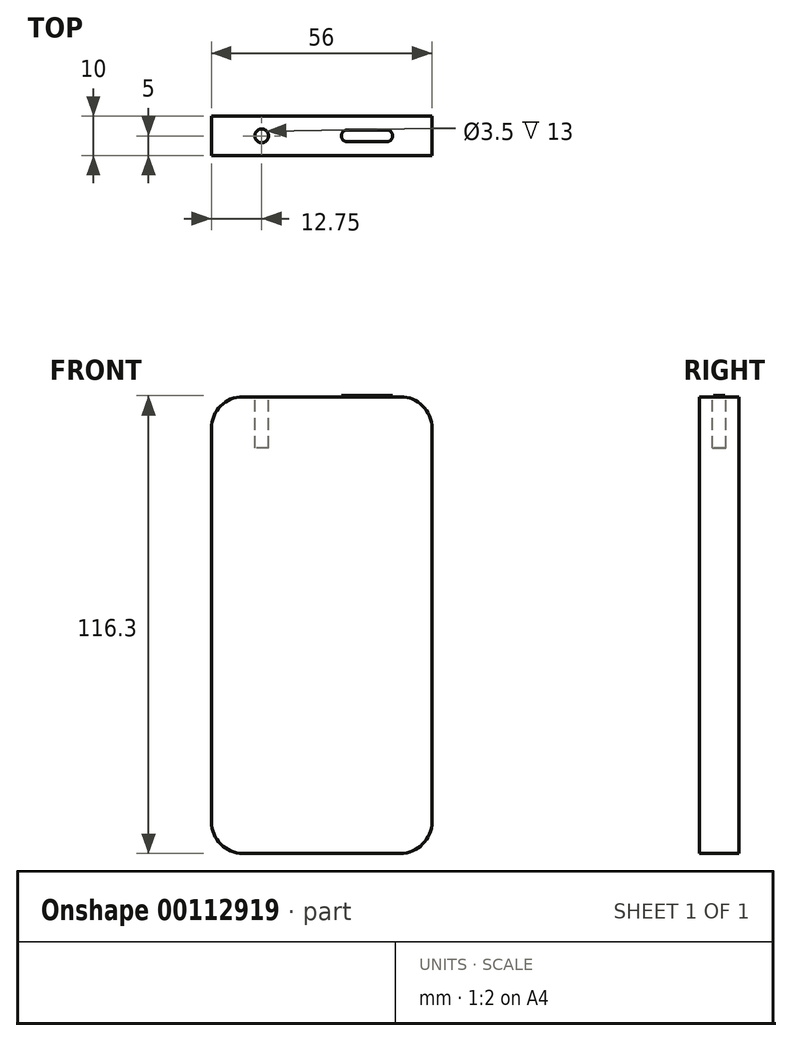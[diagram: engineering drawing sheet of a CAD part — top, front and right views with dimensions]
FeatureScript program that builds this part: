
annotation { "Feature Type Name" : "Feature", "Feature Type Description" : "" }
export const myFeature = defineFeature(function(context is Context, id is Id, definition is map)
    precondition{}
    {
        {
            var Q0;
            Q0=qCreatedBy(makeId("Front.planeOp"),FACE);
            var sketch = newSketch(context, id + "F0", { "sketchPlane" : qUnion([Q0])});
            skLineSegment(sketch, "E0.bottom", {"start": v(28, -58) * mm, "end": v(-28, -58) * mm});
            skLineSegment(sketch, "E0.top", {"start": v(28, 58) * mm, "end": v(-28, 58) * mm});
            skLineSegment(sketch, "E0.left", {"start": v(28, -58) * mm, "end": v(28, 58) * mm});
            skLineSegment(sketch, "E0.right", {"start": v(-28, -58) * mm, "end": v(-28, 58) * mm});
            skPoint(sketch, "E0.middle", {"position": v(0, 0) * mm});
            skSolve(sketch);
        }
        {
            var Q0;
            Q0 = qSketchRegion(id + "F0", true);
            extrude(context, id + "F1", {"entities" : qUnion([Q0]), "endBound" : BoundingType.SYMMETRIC, "depth" : 10 * mm});
        }
        {
            var Q0;
            Q0=makeQuery(id+"F1.opExtrude","SWEPT_EDGE",EDGE,{"disambiguationData":[OSD([sQuery(id+"F0.wireOp",EDGE,"E0.top"),sQuery(id+"F0.wireOp",EDGE,"E0.right")])]});
            var Q1;
            Q1=makeQuery(id+"F1.opExtrude","SWEPT_EDGE",EDGE,{"disambiguationData":[OSD([sQuery(id+"F0.wireOp",EDGE,"E0.top"),sQuery(id+"F0.wireOp",EDGE,"E0.left")])]});
            var Q2;
            Q2=makeQuery(id+"F1.opExtrude","SWEPT_EDGE",EDGE,{"disambiguationData":[OSD([sQuery(id+"F0.wireOp",EDGE,"E0.bottom"),sQuery(id+"F0.wireOp",EDGE,"E0.left")])]});
            var Q3;
            Q3=makeQuery(id+"F1.opExtrude","SWEPT_EDGE",EDGE,{"disambiguationData":[OSD([sQuery(id+"F0.wireOp",EDGE,"E0.bottom"),sQuery(id+"F0.wireOp",EDGE,"E0.right")])]});
            fillet(context, id + "F2", {"entities" : qUnion([Q0, Q1, Q2, Q3]), "radius" : 8 * mm, "tangentPropagation" : true, "allowEdgeOverflow" : false});
        }
        {
            var Q0;
            Q0=makeQuery(id+"F1.opExtrude","SWEPT_FACE",FACE,{"disambiguationData":[OSD([sQuery(id+"F0.wireOp",EDGE,"E0.top")])]});
            var sketch = newSketch(context, id + "F3", { "sketchPlane" : qUnion([Q0])});
            skCircle(sketch, "E1", {"center": v(-15.25, 0) * mm, "radius": 1.75 * mm});
            skSolve(sketch);
        }
        {
            var Q0;
            Q0 = qSketchRegion(id + "F3", true);
            extrude(context, id + "F4", {"entities" : qUnion([Q0]), "operationType" : NewBodyOperationType.REMOVE, "oppositeDirection" : true, "depth" : 13 * mm});
        }
        {
            var Q0;
            Q0=makeQuery(id+"F1.opExtrude","SWEPT_FACE",FACE,{"disambiguationData":[OSD([sQuery(id+"F0.wireOp",EDGE,"E0.top")])]});
            var sketch = newSketch(context, id + "F5", { "sketchPlane" : qUnion([Q0])});
            skLineSegment(sketch, "E2.bottom", {"start": v(6.5, 1.5) * mm, "end": v(16.5, 1.5) * mm});
            skLineSegment(sketch, "E2.top", {"start": v(6.5, -1.5) * mm, "end": v(16.5, -1.5) * mm});
            skLineSegment(sketch, "E2.left", {"start": v(6.5, 1.5) * mm, "end": v(6.5, -1.5) * mm});
            skLineSegment(sketch, "E2.right", {"start": v(16.5, 1.5) * mm, "end": v(16.5, -1.5) * mm});
            skPoint(sketch, "E2.middle", {"position": v(11.5, 0) * mm});
            skArc(sketch, "E3", {"start": v(6.5, 1.5) * mm, "mid": v(5, 0) * mm, "end": v(6.5, -1.5) * mm});
            skArc(sketch, "E4", {"start": v(16.5, -1.5) * mm, "mid": v(18, 0) * mm, "end": v(16.5, 1.5) * mm});
            skSolve(sketch);
        }
        {
            var Q0;
            Q0 = qSketchRegion(id + "F5", true);
            extrude(context, id + "F6", {"entities" : qUnion([Q0]), "operationType" : NewBodyOperationType.ADD, "depth" : .3 * mm});
        }
    });
